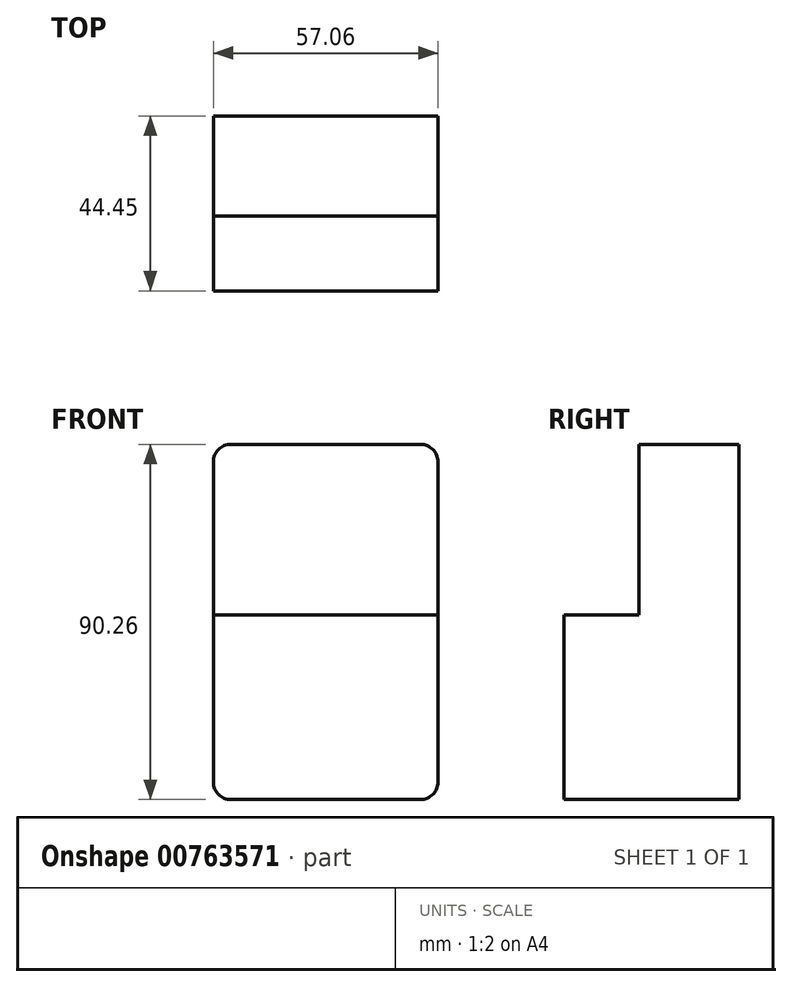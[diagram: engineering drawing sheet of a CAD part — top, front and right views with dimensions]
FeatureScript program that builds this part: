
annotation { "Feature Type Name" : "Feature", "Feature Type Description" : "" }
export const myFeature = defineFeature(function(context is Context, id is Id, definition is map)
    precondition{}
    {
        {
            var Q0;
            Q0=qCreatedBy(makeId("Front.planeOp"),FACE);
            var sketch = newSketch(context, id + "F0", { "sketchPlane" : qUnion([Q0])});
            skLineSegment(sketch, "E0.bottom", {"start": v(-25.7, 43.29) * mm, "end": v(22.46, 43.29) * mm});
            skLineSegment(sketch, "E0.top", {"start": v(-25.7, -46.97) * mm, "end": v(22.46, -46.97) * mm});
            skLineSegment(sketch, "E0.left", {"start": v(-30.15, 38.84) * mm, "end": v(-30.15, -42.52) * mm});
            skLineSegment(sketch, "E0.right", {"start": v(26.9, 38.84) * mm, "end": v(26.9, -42.52) * mm});
            skPoint(sketch, "E1.visualSharp", {"position": v(-30.15, 43.29) * mm});
            skArc(sketch, "E1.filletArc", {"start": v(-25.7, 43.29) * mm, "mid": v(-28.85, 41.99) * mm, "end": v(-30.15, 38.84) * mm});
            skPoint(sketch, "E2.visualSharp", {"position": v(26.9, 43.29) * mm});
            skArc(sketch, "E2.filletArc", {"start": v(26.9, 38.84) * mm, "mid": v(25.6, 41.99) * mm, "end": v(22.46, 43.29) * mm});
            skPoint(sketch, "E3.visualSharp", {"position": v(-30.15, -46.97) * mm});
            skArc(sketch, "E3.filletArc", {"start": v(-30.15, -42.52) * mm, "mid": v(-28.85, -45.67) * mm, "end": v(-25.7, -46.97) * mm});
            skPoint(sketch, "E4.visualSharp", {"position": v(26.9, -46.97) * mm});
            skArc(sketch, "E4.filletArc", {"start": v(22.46, -46.97) * mm, "mid": v(25.6, -45.67) * mm, "end": v(26.9, -42.52) * mm});
            skSolve(sketch);
        }
        {
            var Q0;
            Q0=makeQuery(id+"F0.imprint","IMPRINT",FACE,{"disambiguationData":[TD([[makeQuery(id+"F0.imprint","IMPRINT",EDGE,{"derivedFrom":sQuery(id+"F0.wireOp",EDGE,"E0.bottom")}),-1.0]])]});
            extrude(context, id + "F1", {"entities" : qUnion([Q0]), "depth" : 25.4 * mm, "offsetDistance" : 25.4 * mm});
        }
        {
            var Q0;
            Q0=makeQuery(id+"F1.opExtrude","CAP_FACE",FACE,{"disambiguationData":[OSD([sQuery(id+"F0.wireOp",EDGE,"E0.bottom"),sQuery(id+"F0.wireOp",EDGE,"E0.top"),sQuery(id+"F0.wireOp",EDGE,"E0.left"),sQuery(id+"F0.wireOp",EDGE,"E0.right"),sQuery(id+"F0.wireOp",EDGE,"E1.filletArc"),sQuery(id+"F0.wireOp",EDGE,"E2.filletArc"),sQuery(id+"F0.wireOp",EDGE,"E3.filletArc"),sQuery(id+"F0.wireOp",EDGE,"E4.filletArc")])],"isStart":false});
            var sketch = newSketch(context, id + "F2", { "sketchPlane" : qUnion([Q0])});
            skLineSegment(sketch, "E5.bottom", {"start": v(-30.15, 0) * mm, "end": v(27.13, 0) * mm});
            skLineSegment(sketch, "E5.top", {"start": v(-25.7, -46.97) * mm, "end": v(22.68, -46.97) * mm});
            skLineSegment(sketch, "E5.left", {"start": v(-30.15, 0) * mm, "end": v(-30.15, -42.52) * mm});
            skLineSegment(sketch, "E5.right", {"start": v(27.13, 0) * mm, "end": v(27.13, -42.52) * mm});
            skPoint(sketch, "E6.visualSharp", {"position": v(-30.15, -46.97) * mm});
            skArc(sketch, "E6.filletArc", {"start": v(-30.15, -42.52) * mm, "mid": v(-28.85, -45.67) * mm, "end": v(-25.7, -46.97) * mm});
            skPoint(sketch, "E7.visualSharp", {"position": v(27.13, -46.97) * mm});
            skArc(sketch, "E7.filletArc", {"start": v(22.68, -46.97) * mm, "mid": v(25.83, -45.67) * mm, "end": v(27.13, -42.52) * mm});
            skSolve(sketch);
        }
        {
            var Q0;
            {var subQ1=sQuery(id+"F2.wireOp",EDGE,"E5.left");Q0=makeQuery(id+"F2.imprint","IMPRINT",FACE,{"disambiguationData":[TD([[makeQuery(id+"F2.imprint","IMPRINT",EDGE,{"derivedFrom":subQ1}),1.0]])]});}
            extrude(context, id + "F3", {"entities" : qUnion([Q0]), "operationType" : NewBodyOperationType.ADD, "depth" : 19.05 * mm, "offsetDistance" : 25.4 * mm});
        }
    });
